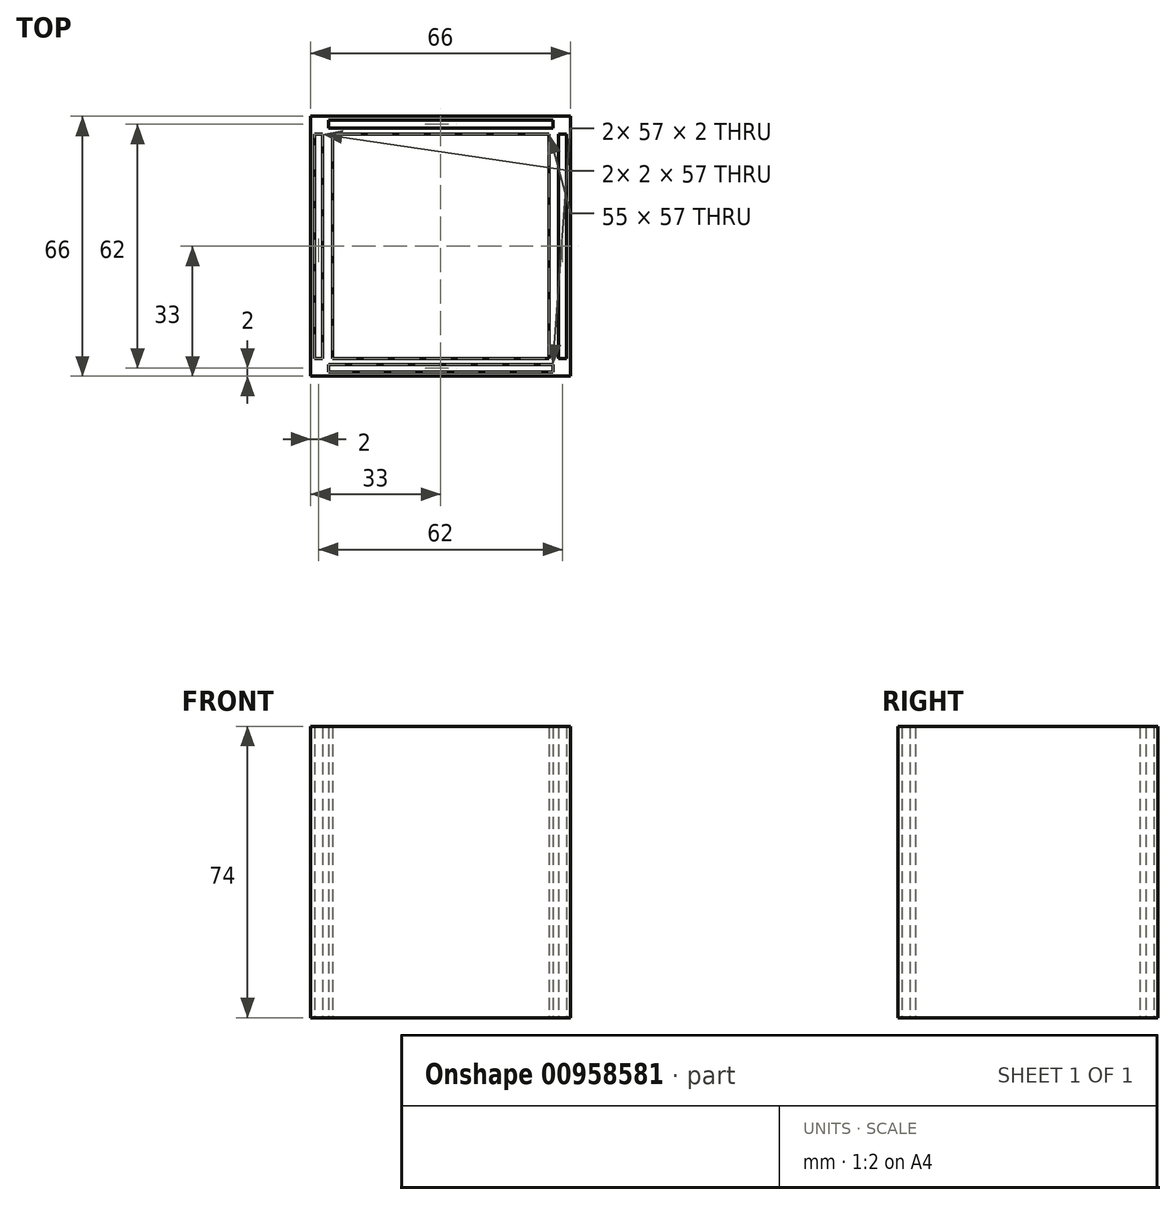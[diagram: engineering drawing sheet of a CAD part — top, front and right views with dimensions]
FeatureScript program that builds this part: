
annotation { "Feature Type Name" : "Feature", "Feature Type Description" : "" }
export const myFeature = defineFeature(function(context is Context, id is Id, definition is map)
    precondition{}
    {
        {
            var Q0;
            Q0=qCreatedBy(makeId("Top.planeOp"),FACE);
            var sketch = newSketch(context, id + "F0", { "sketchPlane" : qUnion([Q0])});
            skLineSegment(sketch, "E0.bottom", {"start": v(33, -33) * mm, "end": v(-33, -33) * mm});
            skLineSegment(sketch, "E0.top", {"start": v(33, 33) * mm, "end": v(-33, 33) * mm});
            skLineSegment(sketch, "E0.left", {"start": v(33, -33) * mm, "end": v(33, 33) * mm});
            skLineSegment(sketch, "E0.right", {"start": v(-33, -33) * mm, "end": v(-33, 33) * mm});
            skPoint(sketch, "E0.middle", {"position": v(0, 0) * mm});
            skPoint(sketch, "E1", {"position": v(-28.5, -33) * mm});
            skPoint(sketch, "E2", {"position": v(-28.5, -32) * mm});
            skLineSegment(sketch, "E3.bottom", {"start": v(-28.5, -32) * mm, "end": v(28.5, -32) * mm});
            skLineSegment(sketch, "E3.top", {"start": v(-28.5, -30) * mm, "end": v(28.5, -30) * mm});
            skLineSegment(sketch, "E3.left", {"start": v(-28.5, -32) * mm, "end": v(-28.5, -30) * mm});
            skLineSegment(sketch, "E3.right", {"start": v(28.5, -32) * mm, "end": v(28.5, -30) * mm});
            skLineSegment(sketch, "E4.MirrorCS", {"start": v(-28.5, 30) * mm, "end": v(28.5, 30) * mm});
            skLineSegment(sketch, "E5.MirrorCS", {"start": v(-28.5, 32) * mm, "end": v(28.5, 32) * mm});
            skLineSegment(sketch, "E6.MirrorCS", {"start": v(-28.5, 32) * mm, "end": v(-28.5, 30) * mm});
            skLineSegment(sketch, "E7.MirrorCS", {"start": v(28.5, 32) * mm, "end": v(28.5, 30) * mm});
            skLineSegment(sketch, "E8.MirrorCS", {"start": v(30, -28.5) * mm, "end": v(30, 28.5) * mm});
            skLineSegment(sketch, "E9.MirrorCS", {"start": v(32, -28.5) * mm, "end": v(32, 28.5) * mm});
            skPoint(sketch, "E10", {"position": v(-27.5, 33) * mm});
            skPoint(sketch, "E11", {"position": v(-33, 28.5) * mm});
            skLineSegment(sketch, "E12.bottom", {"start": v(-27.5, 28.5) * mm, "end": v(27.5, 28.5) * mm});
            skLineSegment(sketch, "E12.top", {"start": v(-27.5, -28.5) * mm, "end": v(27.5, -28.5) * mm});
            skLineSegment(sketch, "E12.left", {"start": v(-27.5, 28.5) * mm, "end": v(-27.5, -28.5) * mm});
            skLineSegment(sketch, "E12.right", {"start": v(27.5, 28.5) * mm, "end": v(27.5, -28.5) * mm});
            skLineSegment(sketch, "E13", {"start": v(30, -28.5) * mm, "end": v(32, -28.5) * mm});
            skLineSegment(sketch, "E14", {"start": v(32, 28.5) * mm, "end": v(30, 28.5) * mm});
            skLineSegment(sketch, "E15.MirrorCS", {"start": v(-32, 28.5) * mm, "end": v(-30, 28.5) * mm});
            skLineSegment(sketch, "E16.MirrorCS", {"start": v(-30, -28.5) * mm, "end": v(-30, 28.5) * mm});
            skLineSegment(sketch, "E17.MirrorCS", {"start": v(-32, -28.5) * mm, "end": v(-32, 28.5) * mm});
            skLineSegment(sketch, "E18.MirrorCS", {"start": v(-30, -28.5) * mm, "end": v(-32, -28.5) * mm});
            skSolve(sketch);
        }
        {
            var Q0;
            Q0=makeQuery(id+"F0.imprint","IMPRINT",FACE,{"disambiguationData":[TD([[makeQuery(id+"F0.imprint","IMPRINT",EDGE,{"derivedFrom":sQuery(id+"F0.wireOp",EDGE,"E0.bottom")}),-1.0]])]});
            extrude(context, id + "F1", {"entities" : qUnion([Q0]), "depth" : 74 * mm, "offsetDistance" : 25 * mm});
        }
    });
